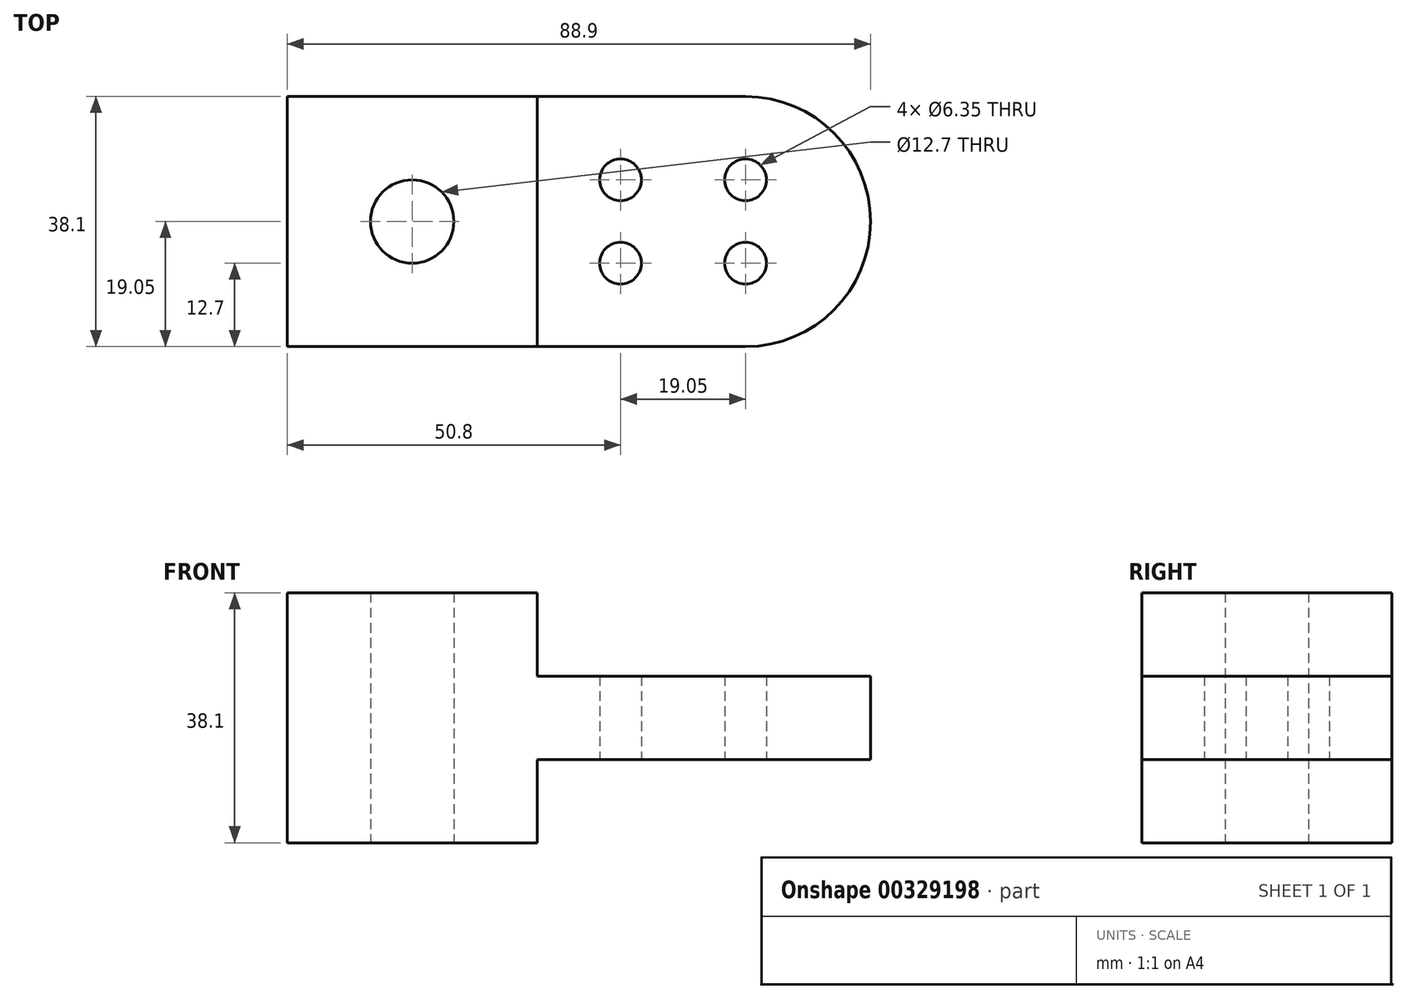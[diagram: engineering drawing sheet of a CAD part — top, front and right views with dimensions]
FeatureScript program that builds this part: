
annotation { "Feature Type Name" : "Feature", "Feature Type Description" : "" }
export const myFeature = defineFeature(function(context is Context, id is Id, definition is map)
    precondition{}
    {
        {
            var Q0;
            Q0=qCreatedBy(makeId("Front.planeOp"),FACE);
            var sketch = newSketch(context, id + "F0", { "sketchPlane" : qUnion([Q0])});
            skLineSegment(sketch, "E0", {"start": v(0, 0) * mm, "end": v(0, 38.1) * mm});
            skLineSegment(sketch, "E1", {"start": v(0, 38.1) * mm, "end": v(38.1, 38.1) * mm});
            skLineSegment(sketch, "E2", {"start": v(38.1, 38.1) * mm, "end": v(38.1, 25.4) * mm});
            skLineSegment(sketch, "E3", {"start": v(38.1, 25.4) * mm, "end": v(88.9, 25.4) * mm});
            skLineSegment(sketch, "E4", {"start": v(88.9, 25.4) * mm, "end": v(88.9, 12.7) * mm});
            skLineSegment(sketch, "E5", {"start": v(88.9, 12.7) * mm, "end": v(38.1, 12.7) * mm});
            skLineSegment(sketch, "E6", {"start": v(38.1, 12.7) * mm, "end": v(38.1, 0) * mm});
            skLineSegment(sketch, "E7", {"start": v(38.1, 0) * mm, "end": v(0, 0) * mm});
            skSolve(sketch);
        }
        {
            var Q0;
            Q0 = qSketchRegion(id + "F0", true);
            extrude(context, id + "F1", {"entities" : qUnion([Q0]), "depth" : 38.1 * mm});
        }
        {
            var Q0;
            Q0=qCreatedBy(makeId("Top.planeOp"),FACE);
            var sketch = newSketch(context, id + "F2", { "sketchPlane" : qUnion([Q0])});
            skCircle(sketch, "E8", {"center": v(19.05, -19.05) * mm, "radius": 6.35 * mm});
            skSolve(sketch);
        }
        {
            var Q0;
            Q0 = qSketchRegion(id + "F2", true);
            extrude(context, id + "F3", {"entities" : qUnion([Q0]), "operationType" : NewBodyOperationType.REMOVE, "endBound" : BoundingType.THROUGH_ALL, "depth" : 25.4 * mm});
        }
        {
            var Q0;
            Q0=qCreatedBy(makeId("Top.planeOp"),FACE);
            var sketch = newSketch(context, id + "F4", { "sketchPlane" : qUnion([Q0])});
            skCircle(sketch, "E9", {"center": v(50.8, -12.7) * mm, "radius": 3.18 * mm});
            skCircle(sketch, "E10", {"center": v(69.85, -12.7) * mm, "radius": 3.18 * mm});
            skCircle(sketch, "E11", {"center": v(50.8, -25.4) * mm, "radius": 3.18 * mm});
            skCircle(sketch, "E12", {"center": v(69.85, -25.4) * mm, "radius": 3.18 * mm});
            skSolve(sketch);
        }
        {
            var Q0;
            Q0 = qSketchRegion(id + "F4", true);
            extrude(context, id + "F5", {"entities" : qUnion([Q0]), "operationType" : NewBodyOperationType.REMOVE, "endBound" : BoundingType.THROUGH_ALL, "depth" : 25.4 * mm});
        }
        {
            var Q0;
            Q0=qCreatedBy(makeId("Top.planeOp"),FACE);
            var sketch = newSketch(context, id + "F6", { "sketchPlane" : qUnion([Q0])});
            skLineSegment(sketch, "E13.0", {"start": v(88.9, 0) * mm, "end": v(69.85, 0) * mm});
            skLineSegment(sketch, "E14.0", {"start": v(88.9, -38.1) * mm, "end": v(88.9, 0) * mm});
            skLineSegment(sketch, "E15.0", {"start": v(69.85, -38.1) * mm, "end": v(88.9, -38.1) * mm});
            skArc(sketch, "E16", {"start": v(69.85, -38.1) * mm, "mid": v(88.9, -19.05) * mm, "end": v(69.85, 0) * mm});
            skPoint(sketch, "E17.orphan", {"position": v(38.1, 0) * mm});
            skPoint(sketch, "E18.orphan", {"position": v(38.1, -38.1) * mm});
            skSolve(sketch);
        }
        {
            var Q0;
            Q0 = qSketchRegion(id + "F6", true);
            extrude(context, id + "F7", {"entities" : qUnion([Q0]), "operationType" : NewBodyOperationType.REMOVE, "depth" : 25.4 * mm});
        }
    });
